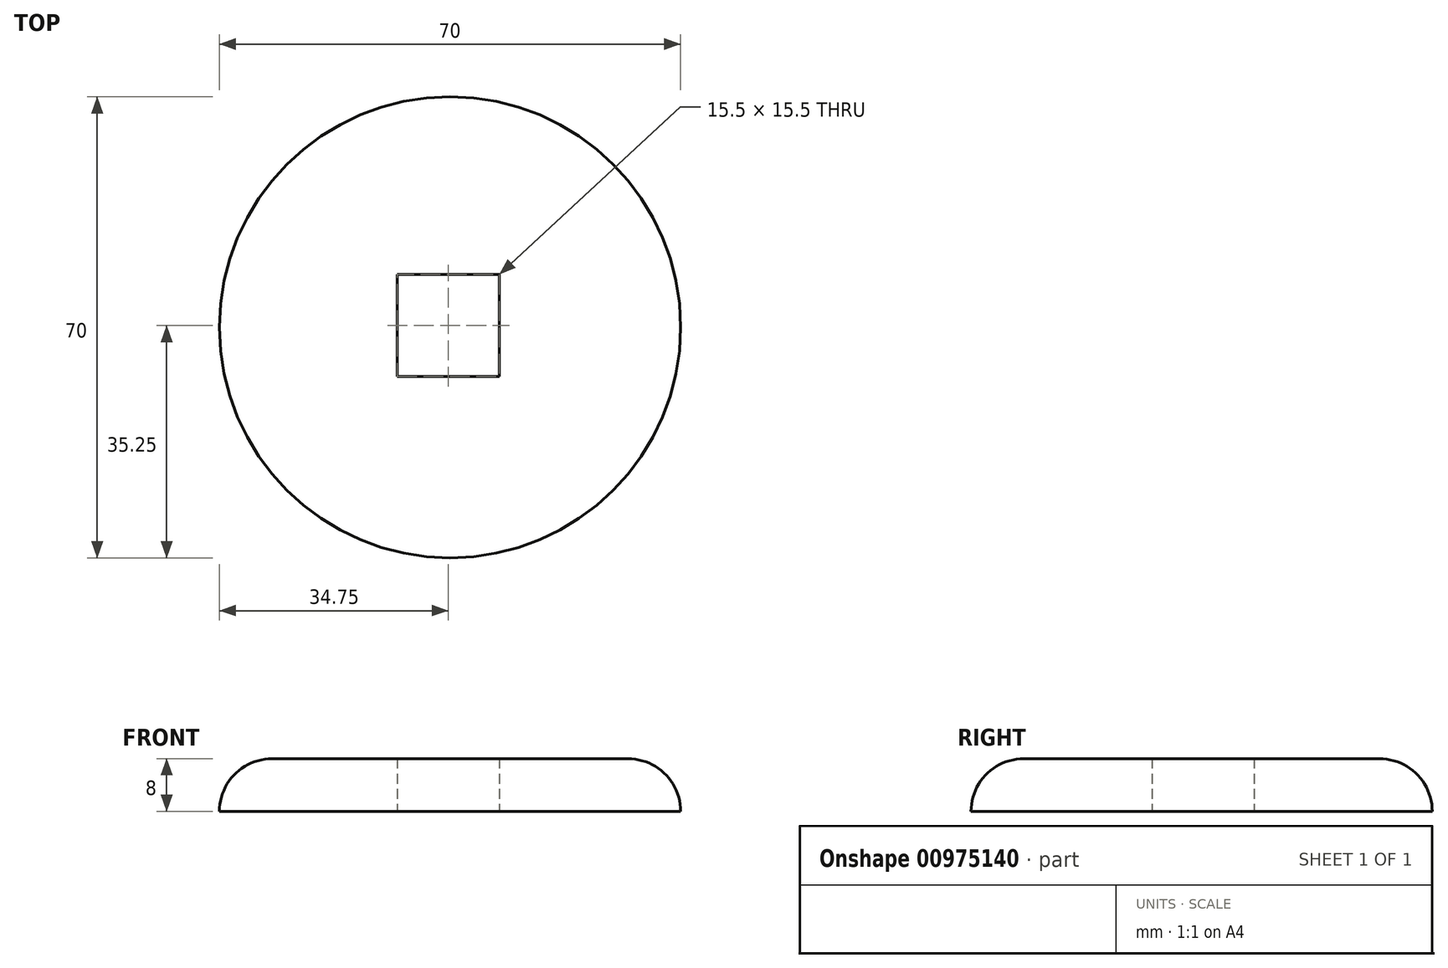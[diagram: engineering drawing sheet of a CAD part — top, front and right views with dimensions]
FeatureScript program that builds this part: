
annotation { "Feature Type Name" : "Feature", "Feature Type Description" : "" }
export const myFeature = defineFeature(function(context is Context, id is Id, definition is map)
    precondition{}
    {
        {
            var Q0;
            Q0=qCreatedBy(makeId("Top.planeOp"),FACE);
            var sketch = newSketch(context, id + "F0", { "sketchPlane" : qUnion([Q0])});
            skCircle(sketch, "E0", {"center": v(0, 0) * mm, "radius": 35 * mm});
            skLineSegment(sketch, "E1.bottom", {"start": v(-8, 8) * mm, "end": v(7.5, 8) * mm});
            skLineSegment(sketch, "E1.top", {"start": v(-8, -7.5) * mm, "end": v(7.5, -7.5) * mm});
            skLineSegment(sketch, "E1.left", {"start": v(-8, 8) * mm, "end": v(-8, -7.5) * mm});
            skLineSegment(sketch, "E1.right", {"start": v(7.5, 8) * mm, "end": v(7.5, -7.5) * mm});
            skSolve(sketch);
        }
        {
            var Q0;
            Q0 = qSketchRegion(id + "F0", true);
            extrude(context, id + "F1", {"entities" : qUnion([Q0]), "depth" : 8 * mm, "offsetDistance" : 25 * mm});
        }
        {
            var Q0;
            Q0=makeQuery(id+"F1.opExtrude","CAP_EDGE",EDGE,{"disambiguationData":[OSD([sQuery(id+"F0.wireOp",EDGE,"E0")])],"isStart":false});
            fillet(context, id + "F2", {"entities" : qUnion([Q0]), "radius" : 8 * mm, "tangentPropagation" : true, "allowEdgeOverflow" : false});
        }
    });
